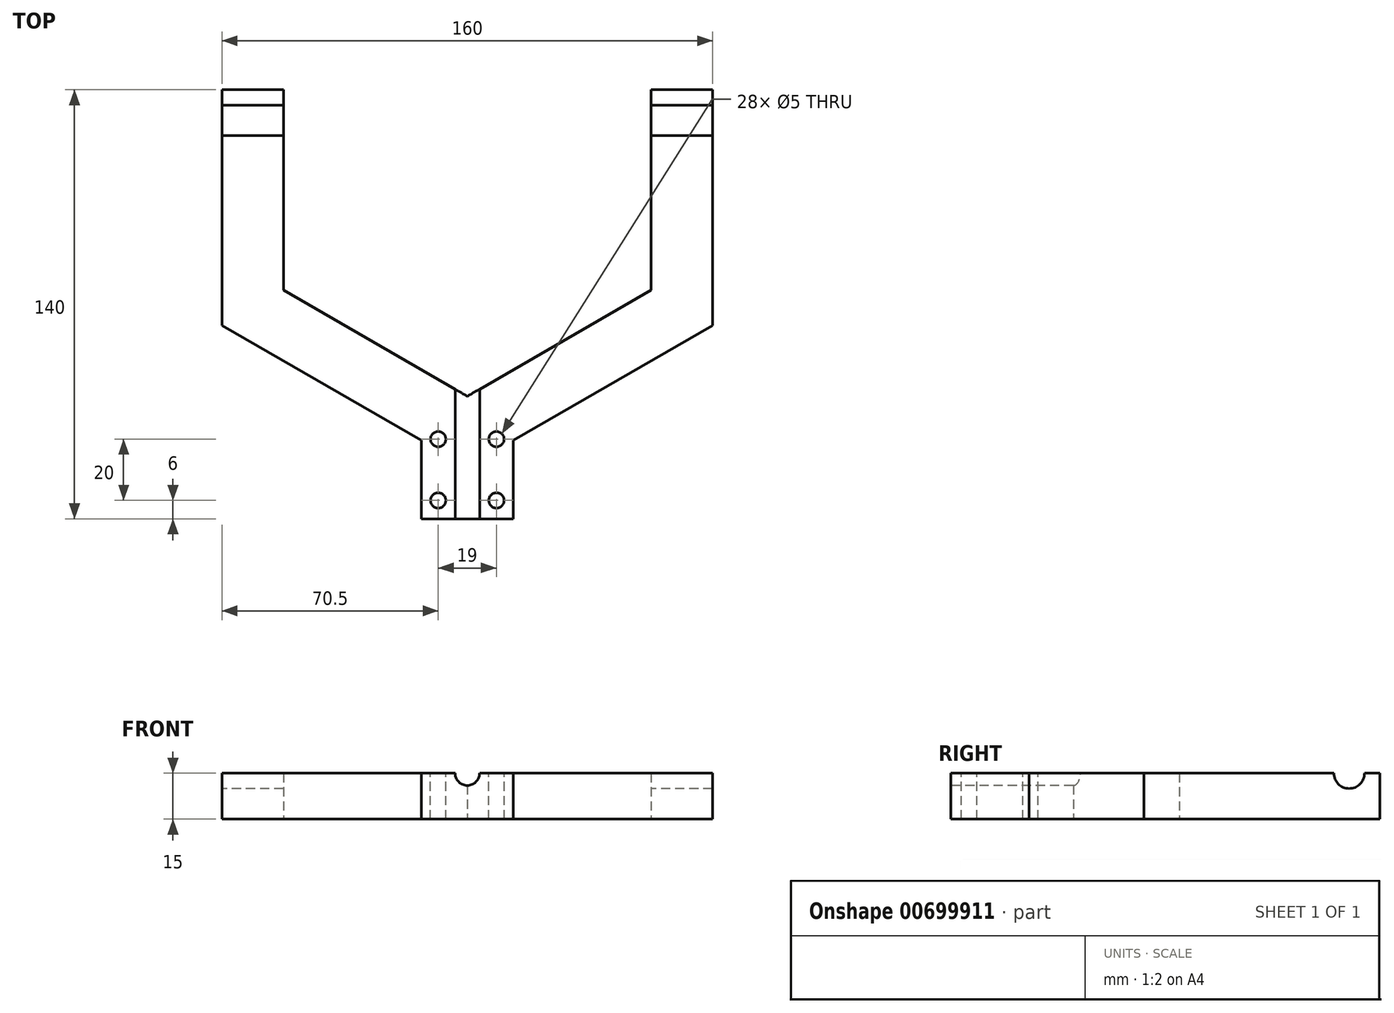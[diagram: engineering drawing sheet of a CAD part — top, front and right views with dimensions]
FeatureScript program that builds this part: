
annotation { "Feature Type Name" : "Feature", "Feature Type Description" : "" }
export const myFeature = defineFeature(function(context is Context, id is Id, definition is map)
    precondition{}
    {
        {
            var Q0;
            Q0=qCreatedBy(makeId("Top.planeOp"),FACE);
            var sketch = newSketch(context, id + "F0", { "sketchPlane" : qUnion([Q0])});
            skLineSegment(sketch, "E0", {"start": v(15, 0) * mm, "end": v(15, 25.57) * mm});
            skLineSegment(sketch, "E1", {"start": v(15, 25.57) * mm, "end": v(80, 63.1) * mm});
            skLineSegment(sketch, "E2", {"start": v(80, 63.1) * mm, "end": v(80, 140) * mm});
            skLineSegment(sketch, "E3", {"start": v(80, 140) * mm, "end": v(60, 140) * mm});
            skLineSegment(sketch, "E4", {"start": v(60, 140) * mm, "end": v(60, 74.64) * mm});
            skLineSegment(sketch, "E5", {"start": v(60, 74.64) * mm, "end": v(0, 40) * mm});
            skLineSegment(sketch, "E6.MirrorCS", {"start": v(-60, 140) * mm, "end": v(-60, 74.64) * mm});
            skLineSegment(sketch, "E7.MirrorCS", {"start": v(-15, 25.57) * mm, "end": v(-80, 63.1) * mm});
            skLineSegment(sketch, "E8.MirrorCS", {"start": v(-15, 0) * mm, "end": v(-15, 25.57) * mm});
            skLineSegment(sketch, "E9.MirrorCS", {"start": v(-80, 63.1) * mm, "end": v(-80, 140) * mm});
            skLineSegment(sketch, "E10.MirrorCS", {"start": v(-80, 140) * mm, "end": v(-60, 140) * mm});
            skLineSegment(sketch, "E11.MirrorCS", {"start": v(-60, 74.64) * mm, "end": v(0, 40) * mm});
            skLineSegment(sketch, "E12", {"start": v(-15, 0) * mm, "end": v(15, 0) * mm});
            skLineSegment(sketch, "E13", {"start": v(60, 74.64) * mm, "end": v(70, 57.32) * mm, "construction": true});
            skSolve(sketch);
        }
        {
            var Q0;
            Q0 = qSketchRegion(id + "F0", true);
            extrude(context, id + "F1", {"entities" : qUnion([Q0]), "depth" : 15 * mm, "offsetDistance" : 25.4 * mm});
        }
        {
            var Q0;
            Q0=makeQuery(id+"F1.opExtrude","SWEPT_FACE",FACE,{"disambiguationData":[OSD([sQuery(id+"F0.wireOp",EDGE,"E12")])]});
            var sketch = newSketch(context, id + "F2", { "sketchPlane" : qUnion([Q0])});
            skArc(sketch, "E14", {"start": v(-4, 15) * mm, "mid": v(0, 11) * mm, "end": v(4, 15) * mm});
            skLineSegment(sketch, "E15", {"start": v(-4, 15) * mm, "end": v(4, 15) * mm});
            skSolve(sketch);
        }
        {
            var Q0;
            Q0=makeQuery(id+"F2.imprint","IMPRINT",FACE,{"disambiguationData":[TD([[makeQuery(id+"F2.imprint","IMPRINT",EDGE,{"derivedFrom":sQuery(id+"F2.wireOp",EDGE,"E14")}),1.0]])]});
            extrude(context, id + "F3", {"entities" : qUnion([Q0]), "operationType" : NewBodyOperationType.REMOVE, "oppositeDirection" : true, "depth" : 50 * mm, "offsetDistance" : 25.4 * mm});
        }
        {
            var Q0;
            Q0=makeQuery(id+"F1.opExtrude","SWEPT_FACE",FACE,{"disambiguationData":[OSD([sQuery(id+"F0.wireOp",EDGE,"E9.MirrorCS")])]});
            var sketch = newSketch(context, id + "F4", { "sketchPlane" : qUnion([Q0])});
            skArc(sketch, "E16", {"start": v(-135, 15) * mm, "mid": v(-130, 10) * mm, "end": v(-125, 15) * mm});
            skLineSegment(sketch, "E17", {"start": v(-125, 15) * mm, "end": v(-135, 15) * mm});
            skSolve(sketch);
        }
        {
            var Q0;
            Q0 = qSketchRegion(id + "F4", true);
            var Q1;
            Q1=makeQuery(id+"F1.opExtrude","SWEPT_FACE",FACE,{"disambiguationData":[OSD([sQuery(id+"F0.wireOp",EDGE,"E2")])]});
            extrude(context, id + "F5", {"entities" : qUnion([Q0]), "operationType" : NewBodyOperationType.REMOVE, "endBound" : BoundingType.UP_TO_SURFACE, "oppositeDirection" : true, "depth" : 25.4 * mm, "endBoundEntityFace" : qUnion([Q1]), "offsetDistance" : 25.4 * mm});
        }
        {
            var Q0;
            {var subQ0=sQuery(id+"F0.wireOp",EDGE,"E9.MirrorCS");var subQ1=sQuery(id+"F0.wireOp",EDGE,"E8.MirrorCS");var subQ2=sQuery(id+"F0.wireOp",EDGE,"E7.MirrorCS");var subQ3=sQuery(id+"F0.wireOp",EDGE,"E6.MirrorCS");var subQ4=sQuery(id+"F0.wireOp",EDGE,"E10.MirrorCS");var subQ5=sQuery(id+"F0.wireOp",EDGE,"E11.MirrorCS");var subQ6=sQuery(id+"F0.wireOp",EDGE,"E12");Q0=makeQuery(id+"F3.boolean.opBoolean","SPLIT",FACE,{"disambiguationData":[TD([makeQuery(id+"F1.opExtrude","SWEPT_FACE",FACE,{"disambiguationData":[OSD([subQ3])]})])],"derivedFrom":makeQuery(id+"F1.opExtrude","CAP_FACE",FACE,{"disambiguationData":[OSD([sQuery(id+"F0.wireOp",EDGE,"E0"),sQuery(id+"F0.wireOp",EDGE,"E1"),sQuery(id+"F0.wireOp",EDGE,"E2"),sQuery(id+"F0.wireOp",EDGE,"E3"),sQuery(id+"F0.wireOp",EDGE,"E4"),sQuery(id+"F0.wireOp",EDGE,"E5"),subQ3,subQ2,subQ1,subQ0,subQ4,subQ5,subQ6])],"isStart":false})});}
            var sketch = newSketch(context, id + "F6", { "sketchPlane" : qUnion([Q0])});
            skCircle(sketch, "E18", {"center": v(-9.5, 6) * mm, "radius": 2.5 * mm});
            skCircle(sketch, "E19", {"center": v(-9.5, 26) * mm, "radius": 2.5 * mm});
            skCircle(sketch, "E20", {"center": v(9.5, 6) * mm, "radius": 2.5 * mm});
            skCircle(sketch, "E21", {"center": v(9.5, 26) * mm, "radius": 2.5 * mm});
            skSolve(sketch);
        }
        {
            var Q0;
            Q0 = qSketchRegion(id + "F6", true);
            extrude(context, id + "F7", {"entities" : qUnion([Q0]), "operationType" : NewBodyOperationType.REMOVE, "endBound" : BoundingType.UP_TO_NEXT, "oppositeDirection" : true, "depth" : 25 * mm, "offsetDistance" : 25 * mm});
        }
    });
